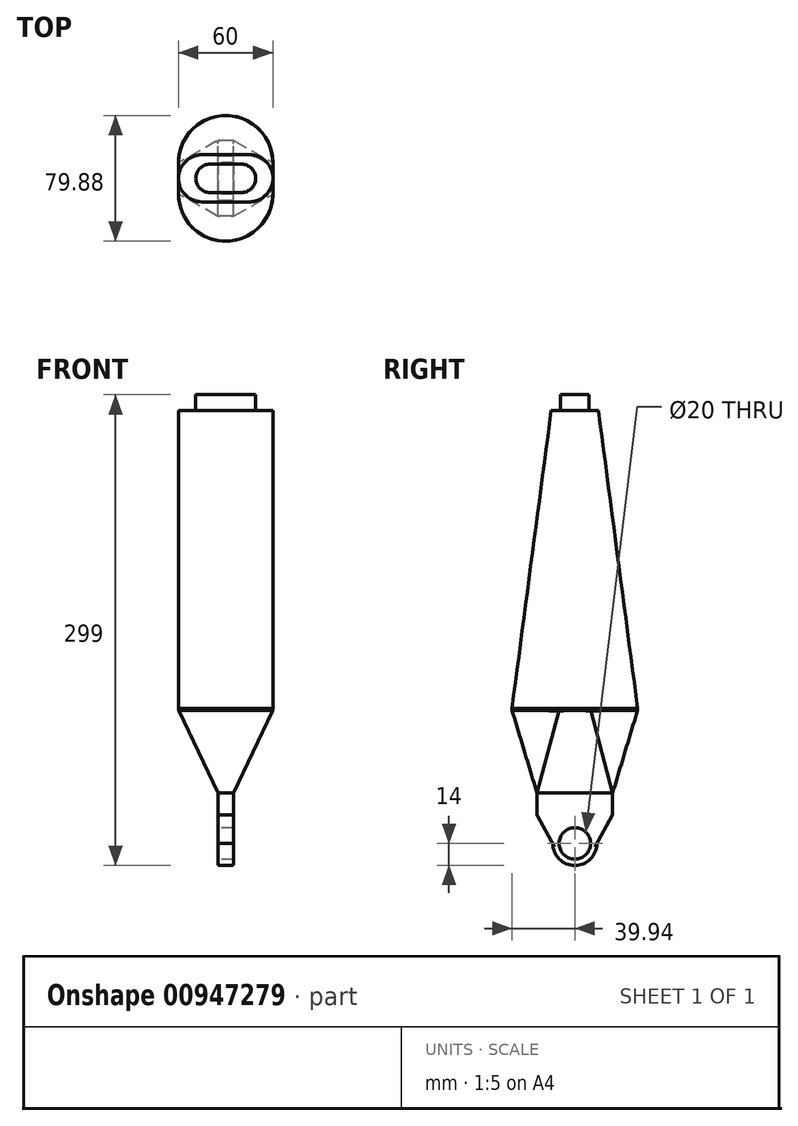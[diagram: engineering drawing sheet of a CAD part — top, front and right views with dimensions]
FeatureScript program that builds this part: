
annotation { "Feature Type Name" : "Feature", "Feature Type Description" : "" }
export const myFeature = defineFeature(function(context is Context, id is Id, definition is map)
    precondition{}
    {
        {
            var Q0;
            Q0=qCreatedBy(makeId("Right.planeOp"),FACE);
            var sketch = newSketch(context, id + "F0", { "sketchPlane" : qUnion([Q0])});
            skCircle(sketch, "E0", {"center": v(0, 0) * mm, "radius": 10 * mm});
            skLineSegment(sketch, "E1.top", {"start": v(-24, 32) * mm, "end": v(24, 32) * mm});
            skLineSegment(sketch, "E1.left", {"start": v(-24, 18) * mm, "end": v(-24, 32) * mm});
            skLineSegment(sketch, "E1.right", {"start": v(24, 18) * mm, "end": v(24, 32) * mm});
            skLineSegment(sketch, "E2", {"start": v(-24, 18) * mm, "end": v(-14, 0) * mm});
            skLineSegment(sketch, "E3", {"start": v(14, 0) * mm, "end": v(24, 18) * mm});
            skArc(sketch, "E4", {"start": v(-14, 0) * mm, "mid": v(0, -14) * mm, "end": v(14, 0) * mm});
            skSolve(sketch);
        }
        {
            var Q0;
            Q0=makeQuery(id+"F0.imprint","IMPRINT",FACE,{"disambiguationData":[TD([[makeQuery(id+"F0.imprint","IMPRINT",EDGE,{"derivedFrom":sQuery(id+"F0.wireOp",EDGE,"E0")}),-1.0]])]});
            extrude(context, id + "F1", {"entities" : qUnion([Q0]), "depth" : 10 * mm, "offsetDistance" : 25 * mm});
        }
        {
            var Q0;
            Q0=makeQuery(id+"F1.opExtrude","CAP_EDGE",EDGE,{"disambiguationData":[OSD([sQuery(id+"F0.wireOp",EDGE,"E4")])],"isStart":true});
            var Q1;
            Q1=makeQuery(id+"F1.opExtrude","CAP_EDGE",EDGE,{"disambiguationData":[OSD([sQuery(id+"F0.wireOp",EDGE,"E4")])],"isStart":false});
            fillet(context, id + "F2", {"entities" : qUnion([Q0, Q1]), "tangentPropagation" : true, "radius" : 1 * mm, "defaultsChanged" : false, "vertexSettings" : [], "allowEdgeOverflow" : false});
        }
        {
            var Q0;
            Q0=qCreatedBy(makeId("Top.planeOp"),FACE);
            cPlane(context, id + "F3", {"entities" : qUnion([Q0]), "cplaneType" : CPlaneType.OFFSET, "offset" : 85 * mm, "width" : 150 * mm, "height" : 150 * mm});
        }
        {
            var Q0;
            Q0=qCreatedBy(id+"F3.planeOp",FACE);
            var sketch = newSketch(context, id + "F4", { "sketchPlane" : qUnion([Q0])});
            skArc(sketch, "E5", {"start": v(35, 10) * mm, "mid": v(5, 40) * mm, "end": v(-25, 10) * mm});
            skArc(sketch, "E6", {"start": v(-25, -10) * mm, "mid": v(5, -40) * mm, "end": v(35, -10) * mm});
            skLineSegment(sketch, "E7", {"start": v(-25, 10) * mm, "end": v(-25, -10) * mm});
            skLineSegment(sketch, "E8", {"start": v(5, 10) * mm, "end": v(5, -10) * mm, "construction": true});
            skLineSegment(sketch, "E9.MirrorCS", {"start": v(-55, 10) * mm, "end": v(-55, -10) * mm, "construction": true});
            skLineSegment(sketch, "E10.MirrorCS", {"start": v(35, 10) * mm, "end": v(35, -10) * mm});
            skSolve(sketch);
        }
        {
            var Q0;
            Q0=makeQuery(id+"F1.opExtrude","SWEPT_FACE",FACE,{"disambiguationData":[OSD([sQuery(id+"F0.wireOp",EDGE,"E1.top")])]});
            var Q1;
            Q1=makeQuery(id+"F4.imprint","IMPRINT",FACE,{"disambiguationData":[TD([[makeQuery(id+"F4.imprint","IMPRINT",EDGE,{"derivedFrom":sQuery(id+"F4.wireOp",EDGE,"E5")}),1.0]])]});
            loft(context, id + "F5", {"operationType" : NewBodyOperationType.ADD, "sheetProfilesArray" : [{ "sheetProfileEntities" : qUnion([Q0]) }, { "sheetProfileEntities" : qUnion([Q1]) }]});
        }
        {
            var Q0;
            Q0=qCreatedBy(id+"F3.planeOp",FACE);
            cPlane(context, id + "F6", {"entities" : qUnion([Q0]), "cplaneType" : CPlaneType.OFFSET, "offset" : 190 * mm, "width" : 150 * mm, "height" : 150 * mm});
        }
        {
            var Q0;
            Q0=qCreatedBy(id+"F6.planeOp",FACE);
            var sketch = newSketch(context, id + "F7", { "sketchPlane" : qUnion([Q0])});
            skArc(sketch, "E11", {"start": v(-10, 15) * mm, "mid": v(-25, 0) * mm, "end": v(-10, -15) * mm});
            skArc(sketch, "E12", {"start": v(20, -15) * mm, "mid": v(35, 0) * mm, "end": v(20, 15) * mm});
            skLineSegment(sketch, "E13", {"start": v(-10, 15) * mm, "end": v(20, 15) * mm});
            skLineSegment(sketch, "E14", {"start": v(-10, -15) * mm, "end": v(20, -15) * mm});
            skSolve(sketch);
        }
        {
            var Q0;
            Q0=makeQuery(id+"F5.opLoft","CAP_FACE",FACE,{"disambiguationData":[OSD([makeQuery(id+"F4.imprint","IMPRINT",FACE,{"disambiguationData":[TD([[makeQuery(id+"F4.imprint","IMPRINT",EDGE,{"derivedFrom":sQuery(id+"F4.wireOp",EDGE,"E5")}),1.0]])]})])],"isStart":true});
            var Q1;
            Q1=makeQuery(id+"F7.imprint","IMPRINT",FACE,{"disambiguationData":[TD([[makeQuery(id+"F7.imprint","IMPRINT",EDGE,{"derivedFrom":sQuery(id+"F7.wireOp",EDGE,"E11")}),1.0]])]});
            loft(context, id + "F8", {"operationType" : NewBodyOperationType.ADD, "sheetProfilesArray" : [{ "sheetProfileEntities" : qUnion([Q0]) }, { "sheetProfileEntities" : qUnion([Q1]) }]});
        }
        {
            var Q0;
            {var subQ0=sQuery(id+"F4.wireOp",EDGE,"E10.MirrorCS");var subQ1=sQuery(id+"F4.wireOp",EDGE,"E7");var subQ2=sQuery(id+"F4.wireOp",EDGE,"E6");Q0=makeQuery(id+"F8.boolean.opBoolean","MERGE",EDGE,{"derivedFrom":[makeQuery(id+"F5.opLoft","MID_CAP_EDGE",EDGE,{"disambiguationData":[OSD([subQ2,subQ1,subQ0])],"capPos":1.0}),makeQuery(id+"F8.opLoft","MID_CAP_EDGE",EDGE,{"disambiguationData":[OSD([subQ2,subQ1,subQ0])],"capPos":0.0})]});}
            var Q1;
            {var subQ0=sQuery(id+"F4.wireOp",EDGE,"E10.MirrorCS");var subQ1=sQuery(id+"F4.wireOp",EDGE,"E7");var subQ2=sQuery(id+"F4.wireOp",EDGE,"E5");Q1=makeQuery(id+"F8.boolean.opBoolean","MERGE",EDGE,{"derivedFrom":[makeQuery(id+"F5.opLoft","MID_CAP_EDGE",EDGE,{"disambiguationData":[OSD([subQ2,subQ1,subQ0])],"capPos":1.0}),makeQuery(id+"F8.opLoft","MID_CAP_EDGE",EDGE,{"disambiguationData":[OSD([subQ2,subQ1,subQ0])],"capPos":0.0})]});}
            var Q2;
            {var subQ0=sQuery(id+"F4.wireOp",EDGE,"E10.MirrorCS");var subQ1=sQuery(id+"F4.wireOp",EDGE,"E6");var subQ2=sQuery(id+"F4.wireOp",EDGE,"E5");Q2=makeQuery(id+"F8.boolean.opBoolean","MERGE",EDGE,{"derivedFrom":[makeQuery(id+"F5.opLoft","MID_CAP_EDGE",EDGE,{"disambiguationData":[OSD([subQ2,subQ1,subQ0])],"capPos":1.0}),makeQuery(id+"F8.opLoft","MID_CAP_EDGE",EDGE,{"disambiguationData":[OSD([subQ2,subQ1,subQ0])],"capPos":0.0})]});}
            var Q3;
            {var subQ0=sQuery(id+"F4.wireOp",EDGE,"E7");var subQ1=sQuery(id+"F4.wireOp",EDGE,"E6");var subQ2=sQuery(id+"F4.wireOp",EDGE,"E5");Q3=makeQuery(id+"F8.boolean.opBoolean","MERGE",EDGE,{"derivedFrom":[makeQuery(id+"F5.opLoft","MID_CAP_EDGE",EDGE,{"disambiguationData":[OSD([subQ2,subQ1,subQ0])],"capPos":1.0}),makeQuery(id+"F8.opLoft","MID_CAP_EDGE",EDGE,{"disambiguationData":[OSD([subQ2,subQ1,subQ0])],"capPos":0.0})]});}
            fillet(context, id + "F9", {"entities" : qUnion([Q0, Q1, Q2, Q3]), "tangentPropagation" : true, "radius" : 3 * mm, "defaultsChanged" : true, "vertexSettings" : [], "allowEdgeOverflow" : false});
        }
        {
            var Q0;
            Q0=makeQuery(id+"F8.opLoft","CAP_FACE",FACE,{"disambiguationData":[OSD([makeQuery(id+"F7.imprint","IMPRINT",FACE,{"disambiguationData":[TD([[makeQuery(id+"F7.imprint","IMPRINT",EDGE,{"derivedFrom":sQuery(id+"F7.wireOp",EDGE,"E11")}),1.0]])]})])],"isStart":true});
            var sketch = newSketch(context, id + "F10", { "sketchPlane" : qUnion([Q0])});
            skArc(sketch, "E15", {"start": v(-5, 9) * mm, "mid": v(-14, 0) * mm, "end": v(-5, -9) * mm});
            skArc(sketch, "E16", {"start": v(15, -9) * mm, "mid": v(24, 0) * mm, "end": v(15, 9) * mm});
            skLineSegment(sketch, "E17", {"start": v(-5, -9) * mm, "end": v(15, -9) * mm});
            skLineSegment(sketch, "E18", {"start": v(-5, 9) * mm, "end": v(15, 9) * mm});
            skSolve(sketch);
        }
        {
            var Q0;
            Q0 = qSketchRegion(id + "F10", true);
            extrude(context, id + "F11", {"entities" : qUnion([Q0]), "operationType" : NewBodyOperationType.ADD, "depth" : 10 * mm, "offsetDistance" : 25 * mm});
        }
    });
